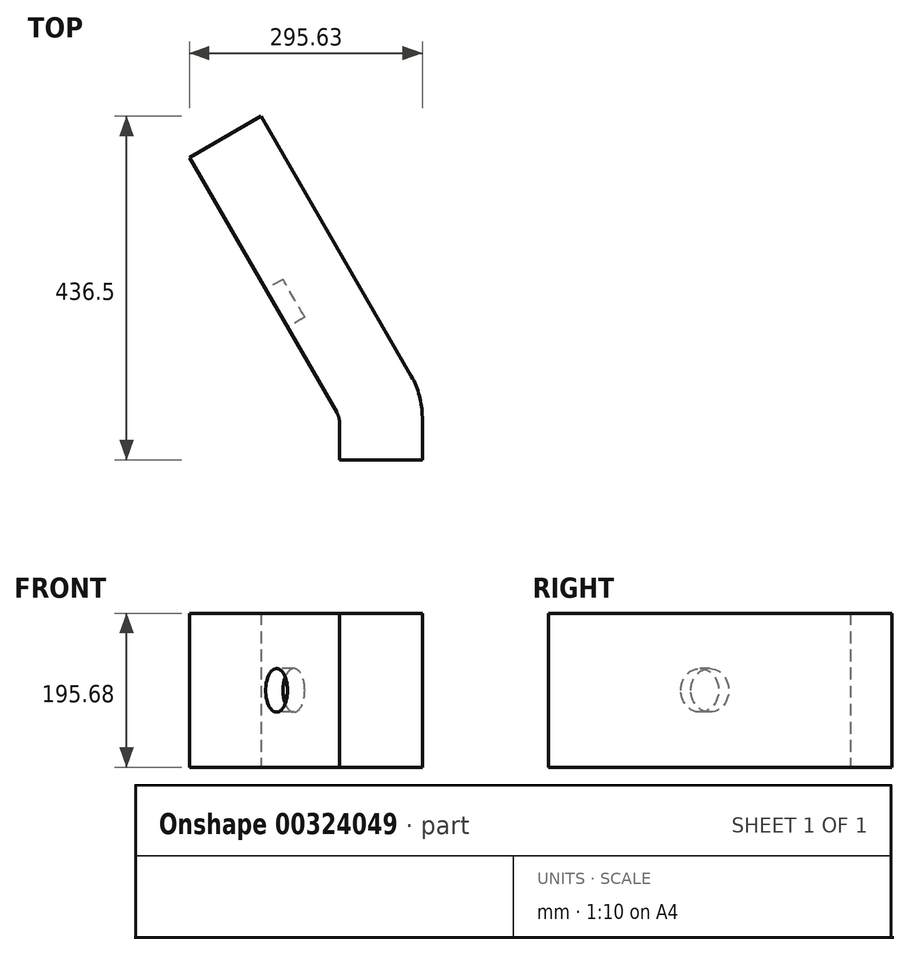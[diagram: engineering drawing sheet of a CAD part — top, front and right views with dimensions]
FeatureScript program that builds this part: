
annotation { "Feature Type Name" : "Feature", "Feature Type Description" : "" }
export const myFeature = defineFeature(function(context is Context, id is Id, definition is map)
    precondition{}
    {
        {
            var Q0;
            Q0=qCreatedBy(makeId("Front.planeOp"),FACE);
            var sketch = newSketch(context, id + "F0", { "sketchPlane" : qUnion([Q0])});
            skLineSegment(sketch, "E0.bottom", {"start": v(32.47, 97.84) * mm, "end": v(-72.66, 97.84) * mm});
            skLineSegment(sketch, "E0.top", {"start": v(32.47, -97.84) * mm, "end": v(-72.66, -97.84) * mm});
            skLineSegment(sketch, "E0.left", {"start": v(32.47, 97.84) * mm, "end": v(32.47, -97.84) * mm});
            skLineSegment(sketch, "E0.right", {"start": v(-72.66, 97.84) * mm, "end": v(-72.66, -97.84) * mm});
            skPoint(sketch, "E0.middle", {"position": v(-20.1, 0) * mm});
            skSolve(sketch);
        }
        {
            var Q0;
            Q0=makeQuery(id+"F0.imprint","IMPRINT",FACE,{"disambiguationData":[TD([[makeQuery(id+"F0.imprint","IMPRINT",EDGE,{"derivedFrom":sQuery(id+"F0.wireOp",EDGE,"E0.bottom")}),1.0]])]});
            extrude(context, id + "F1", {"entities" : qUnion([Q0]), "depth" : 53.97 * mm});
        }
        {
            var Q0;
            Q0=makeQuery(id+"F1.opExtrude","CAP_FACE",FACE,{"disambiguationData":[OSD([sQuery(id+"F0.wireOp",EDGE,"E0.bottom"),sQuery(id+"F0.wireOp",EDGE,"E0.top"),sQuery(id+"F0.wireOp",EDGE,"E0.left"),sQuery(id+"F0.wireOp",EDGE,"E0.right")])],"isStart":true});
            var Q1;
            Q1=makeQuery(id+"F1.opExtrude","CAP_EDGE",EDGE,{"disambiguationData":[OSD([sQuery(id+"F0.wireOp",EDGE,"E0.right")])],"isStart":true});
            revolve(context, id + "F2", {"operationType" : NewBodyOperationType.ADD, "entities" : qUnion([Q0]), "axis" : qUnion([Q1]), "revolveType" : RevolveType.ONE_DIRECTION, "oppositeDirection" : true, "angle" : 30 * degree});
        }
        {
            var Q0;
            Q0=makeQuery(id+"F2.opRevolve","CAP_FACE",FACE,{"disambiguationData":[OSD([sQuery(id+"F0.wireOp",EDGE,"E0.bottom"),sQuery(id+"F0.wireOp",EDGE,"E0.top"),sQuery(id+"F0.wireOp",EDGE,"E0.left"),sQuery(id+"F0.wireOp",EDGE,"E0.right")])],"isStart":false});
            extrude(context, id + "F3", {"entities" : qUnion([Q0]), "operationType" : NewBodyOperationType.ADD, "depth" : 381 * mm});
        }
        {
            var Q0;
            {var subQ0=sQuery(id+"F0.wireOp",EDGE,"E0.right");Q0=makeQuery(id+"F3.boolean.opBoolean","MERGE",EDGE,{"derivedFrom":[makeQuery(id+"F2.boolean.opBoolean","MERGE",EDGE,{"derivedFrom":[makeQuery(id+"F1.opExtrude","CAP_EDGE",EDGE,{"disambiguationData":[OSD([subQ0])],"isStart":true}),makeQuery(id+"F2.opRevolve","CAP_EDGE",EDGE,{"disambiguationData":[OSD([subQ0])],"isStart":true})]}),makeQuery(id+"F3.opExtrude","CAP_EDGE",EDGE,{"disambiguationData":[OSD([subQ0])],"isStart":true})]});}
            fillet(context, id + "F4", {"entities" : qUnion([Q0]), "radius" : 25.4 * mm, "tangentPropagation" : true, "allowEdgeOverflow" : false});
        }
        {
            var Q0;
            Q0=makeQuery(id+"F3.opExtrude","SWEPT_FACE",FACE,{"disambiguationData":[OSD([sQuery(id+"F0.wireOp",EDGE,"E0.right")])]});
            var sketch = newSketch(context, id + "F5", { "sketchPlane" : qUnion([Q0])});
            skCircle(sketch, "E1", {"center": v(-196.32, 0) * mm, "radius": 27.73 * mm});
            skSolve(sketch);
        }
        {
            var Q0;
            Q0=makeQuery(id+"F5.imprint","IMPRINT",FACE,{"disambiguationData":[TD([[makeQuery(id+"F5.imprint","IMPRINT",EDGE,{"derivedFrom":sQuery(id+"F5.wireOp",EDGE,"E1")}),1.0]])]});
            var Q1;
            Q1=sQuery(id+"F5.wireOp",EDGE,"E1");
            extrude(context, id + "F6", {"entities" : qUnion([Q0]), "operationType" : NewBodyOperationType.REMOVE, "surfaceEntities" : qUnion([Q1]), "oppositeDirection" : true, "depth" : 25.4 * mm});
        }
    });
